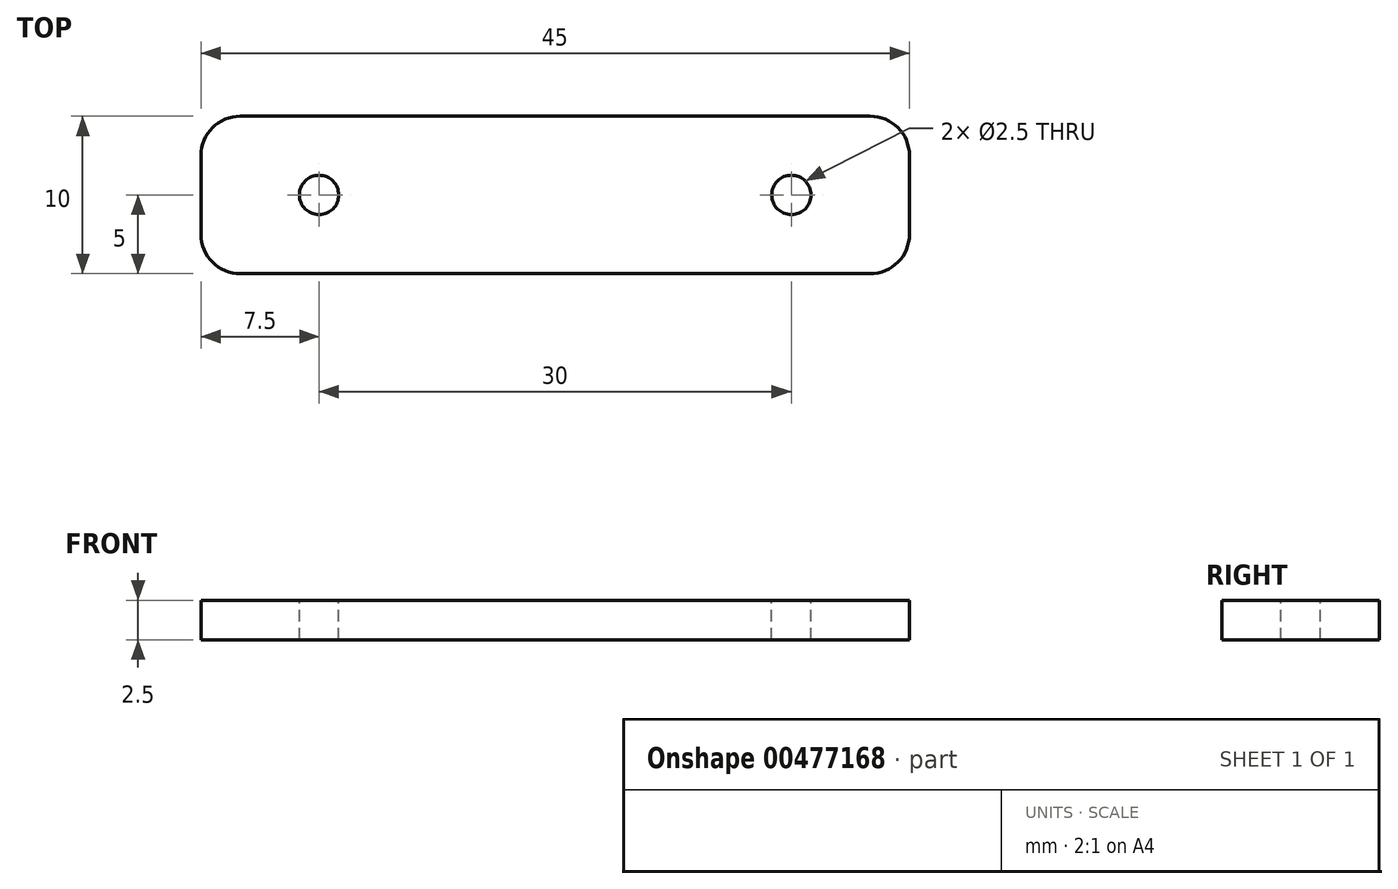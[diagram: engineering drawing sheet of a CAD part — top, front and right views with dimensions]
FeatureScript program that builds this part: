
annotation { "Feature Type Name" : "Feature", "Feature Type Description" : "" }
export const myFeature = defineFeature(function(context is Context, id is Id, definition is map)
    precondition{}
    {
        {
            var Q0;
            Q0=qCreatedBy(makeId("Top.planeOp"),FACE);
            var sketch = newSketch(context, id + "F0", { "sketchPlane" : qUnion([Q0])});
            skLineSegment(sketch, "E0.bottom", {"start": v(-45, 10) * mm, "end": v(45, 10) * mm});
            skLineSegment(sketch, "E0.top", {"start": v(-45, -10) * mm, "end": v(45, -10) * mm});
            skLineSegment(sketch, "E0.left", {"start": v(-45, 10) * mm, "end": v(-45, -10) * mm});
            skLineSegment(sketch, "E0.right", {"start": v(45, 10) * mm, "end": v(45, -10) * mm});
            skPoint(sketch, "E0.middle", {"position": v(0, 0) * mm});
            skSolve(sketch);
        }
        {
            var Q0;
            Q0=makeQuery(id+"F0.imprint","IMPRINT",FACE,{"disambiguationData":[TD([[makeQuery(id+"F0.imprint","IMPRINT",EDGE,{"derivedFrom":sQuery(id+"F0.wireOp",EDGE,"E0.bottom")}),-1.0]])]});
            extrude(context, id + "F1", {"entities" : qUnion([Q0]), "depth" : 5 * mm});
        }
        {
            var Q0;
            Q0=makeQuery(id+"F1.opExtrude","CAP_FACE",FACE,{"disambiguationData":[OSD([sQuery(id+"F0.wireOp",EDGE,"E0.bottom"),sQuery(id+"F0.wireOp",EDGE,"E0.top"),sQuery(id+"F0.wireOp",EDGE,"E0.left"),sQuery(id+"F0.wireOp",EDGE,"E0.right")])],"isStart":false});
            var sketch = newSketch(context, id + "F2", { "sketchPlane" : qUnion([Q0])});
            skCircle(sketch, "E1", {"center": v(-30, 0) * mm, "radius": 2.5 * mm});
            skCircle(sketch, "E2", {"center": v(30, 0) * mm, "radius": 2.5 * mm});
            skSolve(sketch);
        }
        {
            var Q0;
            Q0 = qSketchRegion(id + "F2", true);
            extrude(context, id + "F3", {"entities" : qUnion([Q0]), "operationType" : NewBodyOperationType.REMOVE, "oppositeDirection" : true, "depth" : 5 * mm});
        }
        {
            var Q0;
            Q0=makeQuery(id+"F1.opExtrude","SWEPT_EDGE",EDGE,{"disambiguationData":[OSD([sQuery(id+"F0.wireOp",EDGE,"E0.bottom"),sQuery(id+"F0.wireOp",EDGE,"E0.left")])]});
            var Q1;
            Q1=makeQuery(id+"F1.opExtrude","SWEPT_EDGE",EDGE,{"disambiguationData":[OSD([sQuery(id+"F0.wireOp",EDGE,"E0.top"),sQuery(id+"F0.wireOp",EDGE,"E0.left")])]});
            var Q2;
            Q2=makeQuery(id+"F1.opExtrude","SWEPT_EDGE",EDGE,{"disambiguationData":[OSD([sQuery(id+"F0.wireOp",EDGE,"E0.top"),sQuery(id+"F0.wireOp",EDGE,"E0.right")])]});
            var Q3;
            Q3=makeQuery(id+"F1.opExtrude","SWEPT_EDGE",EDGE,{"disambiguationData":[OSD([sQuery(id+"F0.wireOp",EDGE,"E0.bottom"),sQuery(id+"F0.wireOp",EDGE,"E0.right")])]});
            fillet(context, id + "F4", {"entities" : qUnion([Q0, Q1, Q2, Q3]), "radius" : 5 * mm, "tangentPropagation" : true, "allowEdgeOverflow" : false});
        }
        {
            var Q0;
            Q0=makeQuery(id+"F1.opExtrude","SWEPT_BODY",BODY,{"disambiguationData":[OSD([sQuery(id+"F0.wireOp",EDGE,"E0.bottom"),sQuery(id+"F0.wireOp",EDGE,"E0.top"),sQuery(id+"F0.wireOp",EDGE,"E0.left"),sQuery(id+"F0.wireOp",EDGE,"E0.right")])]});
            var Q1;
            Q1=qCreatedBy(makeId("Origin.pointOp"),VERTEX);
            transform(context, id + "F5", {"entities" : qUnion([Q0]), "transformType" : TransformType.SCALE_UNIFORMLY, "scale" : 0.5, "scalePoint" : qUnion([Q1]), "makeCopy" : false});
        }
    });
